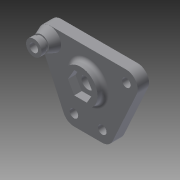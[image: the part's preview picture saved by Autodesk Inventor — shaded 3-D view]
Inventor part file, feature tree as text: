
AUTODESK INVENTOR PART (.ipt)
format: ipt  version: 2013 (Build 170138000, 138)  size: 193,536 bytes
history: native  units: in
note: dims shown in document units (in); Inventor stores cm internally (conversion verified against a paired STEP export)
features: extrude x6, sketch x6, fillet x2, draft x1
ambient origin geometry x8: Origin, YZ Plane, XZ Plane, XY Plane, X Axis, Y Axis, Z Axis, Center Point
bodies: Solid1 (feature_tree)
feature tree (15):
  extrude  "Extrusion1"  Depth=0.2953in
  extrude  "Extrusion2"  Depth=1.5433in
  fillet  "Fillet1"  Radius=0.1772in
  extrude  "Extrusion3"  Depth=1.7717in
  extrude  "Extrusion4"  Depth=0.7972in
  extrude  "Extrusion5"  Depth=0.1772in
  extrude  "Extrusion6"  Depth=0.2362in TaperAngle=0.0deg
  fillet  "Fillet2"  Radius=0.5118in
  draft  "FaceDraft1"
  sketch  "Sketch1"  dims[d0=0.2756in d1=0.2953in]
  sketch  "Sketch2"  dims[d2=0.2953in d3=1.5433in d4=0.1772in]
  sketch  "Sketch3"  dims[d5=0.1772in d6=1.7717in]
  sketch  "Sketch4"  dims[d7=0.7972in d8=0.7972in]
  sketch  "Sketch5"  dims[d9=0.1772in d10=0.1772in]
  sketch  "Sketch6"  dims[d11=0.2362in d12=0.2362in d13=0.0in d14=0.5118in d15=0.1772in d16=0.0in d17=0.1181in d18=0.3248in d19=0.1772in d20=0.0in d21=0.2756in d22=0.0591in d23=0.0in d24=0.3248in d25=0.0984in d26=0.0in d27=0.4724in d28=0.2362in d29=0.4724in d30=0.4724in d31=0.4567in d32=0.7087in d33=0.1575in d34=0.0in d35=0.0787in d36=0.1772in d37=0.1512in]
